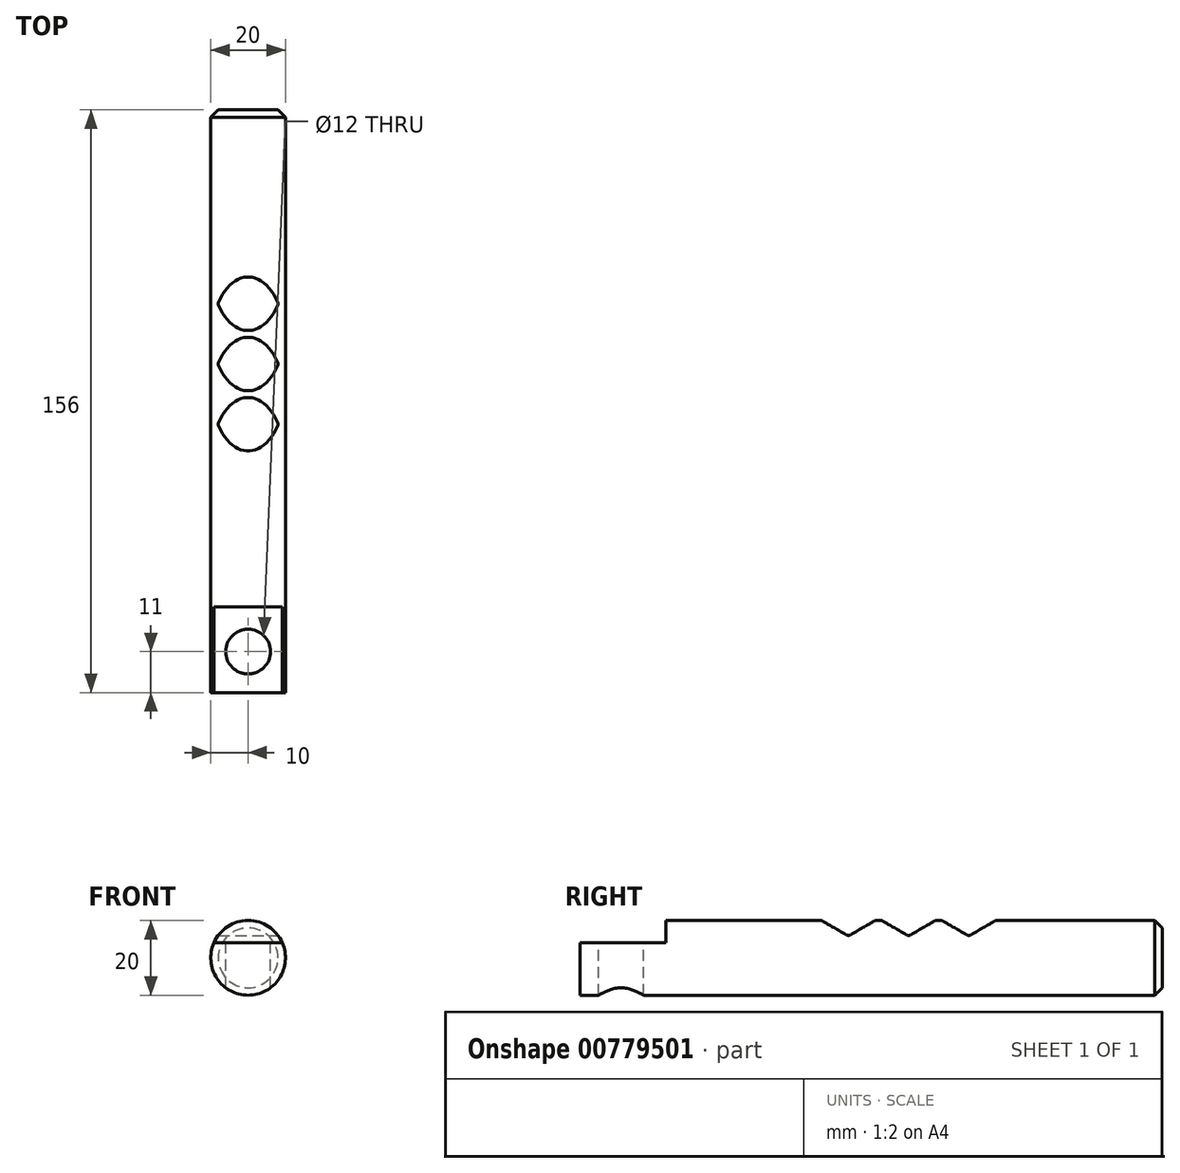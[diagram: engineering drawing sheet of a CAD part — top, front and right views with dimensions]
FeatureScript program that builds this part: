
annotation { "Feature Type Name" : "Feature", "Feature Type Description" : "" }
export const myFeature = defineFeature(function(context is Context, id is Id, definition is map)
    precondition{}
    {
        {
            var Q0;
            Q0=qCreatedBy(makeId("Front.planeOp"),FACE);
            var sketch = newSketch(context, id + "F0", { "sketchPlane" : qUnion([Q0])});
            skCircle(sketch, "E0", {"center": v(0, 0) * mm, "radius": 10 * mm});
            skSolve(sketch);
        }
        {
            var Q0;
            Q0 = qSketchRegion(id + "F0", true);
            extrude(context, id + "F1", {"entities" : qUnion([Q0]), "oppositeDirection" : true, "depth" : 156 * mm, "offsetDistance" : 25 * mm});
        }
        {
            var Q0;
            Q0=makeQuery(id+"F1.opExtrude","CAP_EDGE",EDGE,{"disambiguationData":[OSD([sQuery(id+"F0.wireOp",EDGE,"E0")])],"isStart":false});
            chamfer(context, id + "F2", {"entities" : qUnion([Q0]), "width" : 2 * mm, "tangentPropagation" : true});
        }
        {
            var Q0;
            Q0=qCreatedBy(makeId("Front.planeOp"),FACE);
            var sketch = newSketch(context, id + "F3", { "sketchPlane" : qUnion([Q0])});
            skLineSegment(sketch, "E1.bottom", {"start": v(10, 4) * mm, "end": v(-10, 4) * mm});
            skLineSegment(sketch, "E1.top", {"start": v(10, 12) * mm, "end": v(-10, 12) * mm});
            skLineSegment(sketch, "E1.left", {"start": v(10, 4) * mm, "end": v(10, 12) * mm});
            skLineSegment(sketch, "E1.right", {"start": v(-10, 4) * mm, "end": v(-10, 12) * mm});
            skPoint(sketch, "E1.middle", {"position": v(0, 8) * mm});
            skSolve(sketch);
        }
        {
            var Q0;
            Q0 = qSketchRegion(id + "F3", true);
            extrude(context, id + "F4", {"entities" : qUnion([Q0]), "operationType" : NewBodyOperationType.REMOVE, "oppositeDirection" : true, "depth" : 23 * mm, "offsetDistance" : 25 * mm});
        }
        {
            var Q0;
            Q0=qCreatedBy(makeId("Top.planeOp"),FACE);
            var sketch = newSketch(context, id + "F5", { "sketchPlane" : qUnion([Q0])});
            skCircle(sketch, "E2", {"center": v(0, 11) * mm, "radius": 6 * mm});
            skSolve(sketch);
        }
        {
            var Q0;
            Q0 = qSketchRegion(id + "F5", true);
            extrude(context, id + "F6", {"entities" : qUnion([Q0]), "operationType" : NewBodyOperationType.REMOVE, "endBound" : BoundingType.THROUGH_ALL, "oppositeDirection" : true, "depth" : 25 * mm, "offsetDistance" : 25 * mm, "hasSecondDirection" : true, "secondDirectionBound" : BoundingType.THROUGH_ALL, "secondDirectionOppositeDirection" : false, "secondDirectionDepth" : 25 * mm});
        }
        {
            var Q0;
            Q0=qCreatedBy(makeId("Right.planeOp"),FACE);
            var sketch = newSketch(context, id + "F7", { "sketchPlane" : qUnion([Q0])});
            skLineSegment(sketch, "E3", {"start": v(79.94, 10.5) * mm, "end": v(87.5, 6.13) * mm});
            skLineSegment(sketch, "E4", {"start": v(88.5, 6.13) * mm, "end": v(96.06, 10.5) * mm});
            skLineSegment(sketch, "E5", {"start": v(96.06, 10.5) * mm, "end": v(79.94, 10.5) * mm});
            skLineSegment(sketch, "E6", {"start": v(88, 5.85) * mm, "end": v(88, 10.5) * mm, "construction": true});
            skPoint(sketch, "E7.visualSharp", {"position": v(88, 5.85) * mm});
            skArc(sketch, "E7.filletArc", {"start": v(87.5, 6.13) * mm, "mid": v(88, 6) * mm, "end": v(88.5, 6.13) * mm});
            skLineSegment(sketch, "E8", {"start": v(96.06, 10.5) * mm, "end": v(103.62, 6.13) * mm});
            skLineSegment(sketch, "E9", {"start": v(104.62, 6.13) * mm, "end": v(112.19, 10.5) * mm});
            skLineSegment(sketch, "E10", {"start": v(112.19, 10.5) * mm, "end": v(96.06, 10.5) * mm});
            skLineSegment(sketch, "E11", {"start": v(79.94, 10.5) * mm, "end": v(72.38, 6.13) * mm});
            skLineSegment(sketch, "E12", {"start": v(71.38, 6.13) * mm, "end": v(63.81, 10.5) * mm});
            skLineSegment(sketch, "E13", {"start": v(63.81, 10.5) * mm, "end": v(79.94, 10.5) * mm});
            skLineSegment(sketch, "E14", {"start": v(104.12, 5.85) * mm, "end": v(104.12, 10.5) * mm, "construction": true});
            skLineSegment(sketch, "E15", {"start": v(71.88, 5.85) * mm, "end": v(71.88, 10.5) * mm, "construction": true});
            skPoint(sketch, "E16.visualSharp", {"position": v(71.88, 5.85) * mm});
            skArc(sketch, "E16.filletArc", {"start": v(71.38, 6.13) * mm, "mid": v(71.88, 6) * mm, "end": v(72.38, 6.13) * mm});
            skPoint(sketch, "E17.visualSharp", {"position": v(104.12, 5.85) * mm});
            skArc(sketch, "E17.filletArc", {"start": v(103.62, 6.13) * mm, "mid": v(104.12, 6) * mm, "end": v(104.62, 6.13) * mm});
            skSolve(sketch);
        }
        {
            var Q0;
            Q0 = qSketchRegion(id + "F7", true);
            extrude(context, id + "F8", {"entities" : qUnion([Q0]), "operationType" : NewBodyOperationType.REMOVE, "endBound" : BoundingType.THROUGH_ALL, "oppositeDirection" : true, "depth" : 25 * mm, "offsetDistance" : 25 * mm, "hasSecondDirection" : true, "secondDirectionBound" : BoundingType.THROUGH_ALL, "secondDirectionOppositeDirection" : false, "secondDirectionDepth" : 25 * mm});
        }
    });
